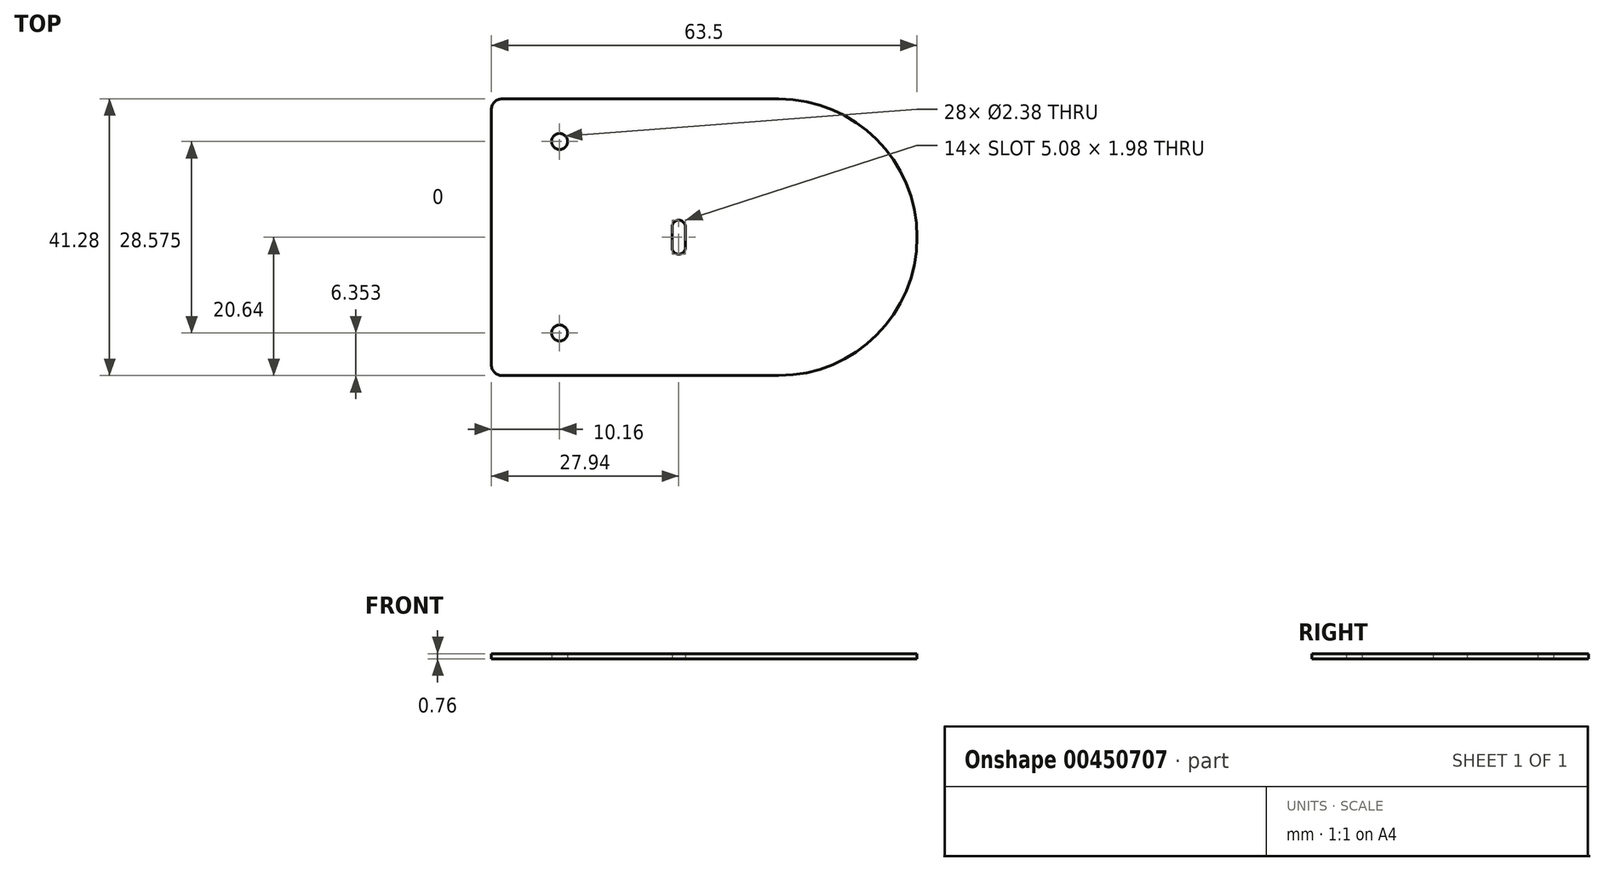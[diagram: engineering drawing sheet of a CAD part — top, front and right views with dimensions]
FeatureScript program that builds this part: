
annotation { "Feature Type Name" : "Feature", "Feature Type Description" : "" }
export const myFeature = defineFeature(function(context is Context, id is Id, definition is map)
    precondition{}
    {
        {
            var Q0;
            Q0=qCreatedBy(makeId("Top.planeOp"),FACE);
            var sketch = newSketch(context, id + "F0", { "sketchPlane" : qUnion([Q0])});
            skLineSegment(sketch, "E0.bottom", {"start": v(11.11, -20.64) * mm, "end": v(-30.16, -20.64) * mm});
            skLineSegment(sketch, "E0.top", {"start": v(11.11, 20.64) * mm, "end": v(-30.16, 20.64) * mm});
            skLineSegment(sketch, "E0.left", {"start": v(31.75, 0) * mm, "end": v(31.75, 0) * mm});
            skLineSegment(sketch, "E0.right", {"start": v(-31.75, -19.05) * mm, "end": v(-31.75, 19.05) * mm});
            skPoint(sketch, "E0.middle", {"position": v(0, 0) * mm});
            skPoint(sketch, "E1.visualSharp", {"position": v(31.75, 20.64) * mm});
            skArc(sketch, "E1.filletArc", {"start": v(31.75, 0) * mm, "mid": v(25.7, 14.6) * mm, "end": v(11.11, 20.64) * mm});
            skPoint(sketch, "E2.visualSharp", {"position": v(31.75, -20.64) * mm});
            skArc(sketch, "E2.filletArc", {"start": v(11.11, -20.64) * mm, "mid": v(25.7, -14.6) * mm, "end": v(31.75, 0) * mm});
            skPoint(sketch, "E3", {"position": v(-31.75, 0) * mm});
            skLineSegment(sketch, "E4.left", {"start": v(-2.82, -1.55) * mm, "end": v(-2.82, 1.55) * mm});
            skLineSegment(sketch, "E4.right", {"start": v(-4.8, -1.55) * mm, "end": v(-4.8, 1.55) * mm});
            skPoint(sketch, "E4.middle", {"position": v(-3.8, 0) * mm});
            skArc(sketch, "E5", {"start": v(-4.8, 1.55) * mm, "mid": v(-3.8, 2.54) * mm, "end": v(-2.82, 1.55) * mm});
            skArc(sketch, "E6", {"start": v(-4.8, -1.55) * mm, "mid": v(-3.8, -2.54) * mm, "end": v(-2.82, -1.55) * mm});
            skPoint(sketch, "E7", {"position": v(-3.8, 2.54) * mm});
            skPoint(sketch, "E8", {"position": v(-3.8, -2.54) * mm});
            skPoint(sketch, "E9.visualSharp", {"position": v(-31.75, 20.64) * mm});
            skArc(sketch, "E9.filletArc", {"start": v(-30.16, 20.64) * mm, "mid": v(-31.29, 20.17) * mm, "end": v(-31.75, 19.05) * mm});
            skPoint(sketch, "E10.visualSharp", {"position": v(-31.75, -20.64) * mm});
            skArc(sketch, "E10.filletArc", {"start": v(-31.75, -19.05) * mm, "mid": v(-31.29, -20.17) * mm, "end": v(-30.16, -20.64) * mm});
            skCircle(sketch, "E11", {"center": v(-21.59, 14.29) * mm, "radius": 1.2 * mm});
            skCircle(sketch, "E12.MirrorC", {"center": v(-21.59, -14.29) * mm, "radius": 1.2 * mm});
            skSolve(sketch);
        }
        {
            var Q0;
            Q0=makeQuery(id+"F0.imprint","IMPRINT",FACE,{"disambiguationData":[TD([[makeQuery(id+"F0.imprint","IMPRINT",EDGE,{"derivedFrom":sQuery(id+"F0.wireOp",EDGE,"E0.bottom")}),-1.0]])]});
            extrude(context, id + "F1", {"entities" : qUnion([Q0]), "depth" : 0.76 * mm});
        }
    });
